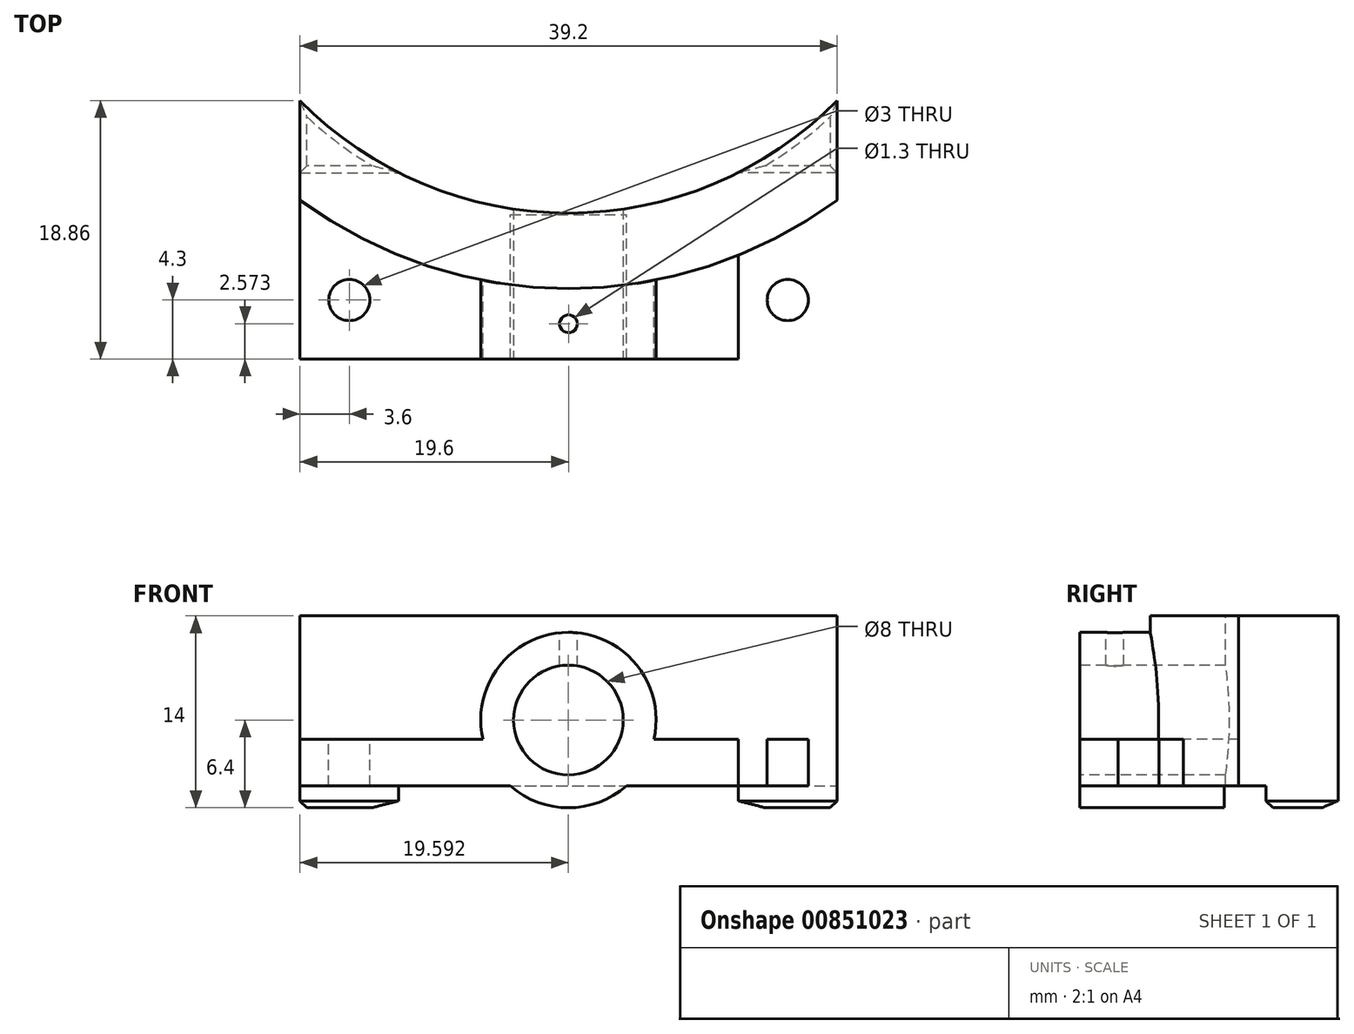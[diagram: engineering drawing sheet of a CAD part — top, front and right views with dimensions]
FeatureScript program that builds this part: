
annotation { "Feature Type Name" : "Feature", "Feature Type Description" : "" }
export const myFeature = defineFeature(function(context is Context, id is Id, definition is map)
    precondition{}
    {
        {
            var Q0;
            Q0=qCreatedBy(makeId("Top.planeOp"),FACE);
            var sketch = newSketch(context, id + "F0", { "sketchPlane" : qUnion([Q0])});
            skLineSegment(sketch, "E0", {"start": v(0, 0) * mm, "end": v(-16, 0) * mm, "construction": true});
            skCircle(sketch, "E1", {"center": v(-16, 0) * mm, "radius": 1.5 * mm});
            skLineSegment(sketch, "E2.bottom", {"start": v(-19.6, 9.3) * mm, "end": v(-12.4, 9.3) * mm});
            skLineSegment(sketch, "E2.top", {"start": v(-19.6, -9.3) * mm, "end": v(-12.4, -9.3) * mm});
            skLineSegment(sketch, "E2.left", {"start": v(-19.6, 9.3) * mm, "end": v(-19.6, -9.3) * mm});
            skLineSegment(sketch, "E2.right", {"start": v(-12.4, 9.3) * mm, "end": v(-12.4, -9.3) * mm});
            skLineSegment(sketch, "E3", {"start": v(0, 0) * mm, "end": v(0, 36.03) * mm, "construction": true});
            skCircle(sketch, "E4.MirrorC", {"center": v(16, 0) * mm, "radius": 1.5 * mm});
            skLineSegment(sketch, "E5.MirrorCS", {"start": v(19.6, 9.3) * mm, "end": v(19.6, -9.3) * mm});
            skLineSegment(sketch, "E6.MirrorCS", {"start": v(19.6, -9.3) * mm, "end": v(12.4, -9.3) * mm});
            skLineSegment(sketch, "E7.MirrorCS", {"start": v(19.6, 9.3) * mm, "end": v(12.4, 9.3) * mm});
            skLineSegment(sketch, "E8.MirrorCS", {"start": v(12.4, 9.3) * mm, "end": v(12.4, -9.3) * mm});
            skArc(sketch, "E9", {"start": v(0, 33.85) * mm, "mid": v(1.84, 32.82) * mm, "end": v(3.6, 31.66) * mm});
            skCircle(sketch, "E10", {"center": v(0, 33.85) * mm, "radius": 27.5 * mm});
            skLineSegment(sketch, "E11", {"start": v(-19.6, -4.3) * mm, "end": v(-12.4, -4.3) * mm});
            skLineSegment(sketch, "E12", {"start": v(-12.4, -4.3) * mm, "end": v(12.4, -4.3) * mm});
            skLineSegment(sketch, "E13", {"start": v(-19.6, 9.3) * mm, "end": v(-19.6, 14.56) * mm});
            skLineSegment(sketch, "E14", {"start": v(19.6, 9.3) * mm, "end": v(19.6, 14.56) * mm});
            skArc(sketch, "E15", {"start": v(-19.6, 7.3) * mm, "mid": v(0, 0.85) * mm, "end": v(19.6, 7.3) * mm});
            skLineSegment(sketch, "E16", {"start": v(12.4, -4.3) * mm, "end": v(19.6, -4.3) * mm});
            skSolve(sketch);
        }
        {
            var Q0;
            Q0=makeQuery(id+"F0.imprint","IMPRINT",FACE,{"disambiguationData":[TD([[makeQuery(id+"F0.imprint","IMPRINT",EDGE,{"derivedFrom":sQuery(id+"F0.wireOp",EDGE,"E1")}),-1.0]])]});
            var Q1;
            {var subQ1=sQuery(id+"F0.wireOp",EDGE,"E2.bottom");var subQ3=sQuery(id+"F0.wireOp",EDGE,"E15");var subQ4=makeQuery(id+"F0.imprint","INTERSECT",VERTEX,{"derivedFrom":[subQ1,subQ3]});Q1=makeQuery(id+"F0.imprint","IMPRINT",FACE,{"disambiguationData":[TD([[makeQuery(id+"F0.imprint","IMPRINT",EDGE,{"disambiguationData":[TD([[subQ4,-1.0]])],"derivedFrom":subQ3}),1.0]])]});}
            var Q2;
            {var subQ0=sQuery(id+"F0.wireOp",EDGE,"E13");var subQ3=sQuery(id+"F0.wireOp",EDGE,"E15");var subQ5=makeQuery(id+"F0.imprint","INTERSECT",VERTEX,{"derivedFrom":[subQ0,subQ3]});Q2=makeQuery(id+"F0.imprint","IMPRINT",FACE,{"disambiguationData":[TD([[makeQuery(id+"F0.imprint","IMPRINT",EDGE,{"disambiguationData":[TD([[subQ5,-1.0]])],"derivedFrom":subQ3}),-1.0]])]});}
            var Q3;
            {var subQ0=sQuery(id+"F0.wireOp",EDGE,"E12");Q3=makeQuery(id+"F0.imprint","IMPRINT",FACE,{"disambiguationData":[TD([[makeQuery(id+"F0.imprint","IMPRINT",EDGE,{"derivedFrom":subQ0}),1.0]])]});}
            var Q4;
            {var subQ1=sQuery(id+"F0.wireOp",EDGE,"E2.right");var subQ3=sQuery(id+"F0.wireOp",EDGE,"E15");var subQ4=makeQuery(id+"F0.imprint","INTERSECT",VERTEX,{"derivedFrom":[subQ1,subQ3]});Q4=makeQuery(id+"F0.imprint","IMPRINT",FACE,{"disambiguationData":[TD([[makeQuery(id+"F0.imprint","IMPRINT",EDGE,{"disambiguationData":[TD([[subQ4,-1.0]])],"derivedFrom":subQ3}),1.0]])]});}
            var Q5;
            {var subQ1=sQuery(id+"F0.wireOp",EDGE,"E7.MirrorCS");var subQ3=sQuery(id+"F0.wireOp",EDGE,"E15");var subQ4=makeQuery(id+"F0.imprint","INTERSECT",VERTEX,{"derivedFrom":[subQ1,subQ3]});Q5=makeQuery(id+"F0.imprint","IMPRINT",FACE,{"disambiguationData":[TD([[makeQuery(id+"F0.imprint","IMPRINT",EDGE,{"disambiguationData":[TD([[subQ4,1.0]])],"derivedFrom":subQ3}),1.0]])]});}
            var Q6;
            {var subQ0=sQuery(id+"F0.wireOp",EDGE,"E14");var subQ3=sQuery(id+"F0.wireOp",EDGE,"E15");var subQ5=makeQuery(id+"F0.imprint","INTERSECT",VERTEX,{"derivedFrom":[subQ0,subQ3]});Q6=makeQuery(id+"F0.imprint","IMPRINT",FACE,{"disambiguationData":[TD([[makeQuery(id+"F0.imprint","IMPRINT",EDGE,{"disambiguationData":[TD([[subQ5,1.0]])],"derivedFrom":subQ3}),-1.0]])]});}
            var Q7;
            Q7=makeQuery(id+"F0.imprint","IMPRINT",FACE,{"disambiguationData":[TD([[makeQuery(id+"F0.imprint","IMPRINT",EDGE,{"derivedFrom":sQuery(id+"F0.wireOp",EDGE,"E4.MirrorC")}),1.0]])]});
            extrude(context, id + "F1", {"entities" : qUnion([Q0, Q1, Q2, Q3, Q4, Q5, Q6, Q7]), "oppositeDirection" : true, "depth" : 3.4 * mm, "offsetDistance" : 25 * mm});
        }
        {
            var Q0;
            {var subQ0=sQuery(id+"F0.wireOp",EDGE,"E2.bottom");Q0=makeQuery(id+"F0.imprint","IMPRINT",FACE,{"disambiguationData":[TD([[makeQuery(id+"F0.imprint","IMPRINT",EDGE,{"derivedFrom":subQ0}),1.0]])]});}
            var Q1;
            {var subQ0=sQuery(id+"F0.wireOp",EDGE,"E7.MirrorCS");Q1=makeQuery(id+"F0.imprint","IMPRINT",FACE,{"disambiguationData":[TD([[makeQuery(id+"F0.imprint","IMPRINT",EDGE,{"derivedFrom":subQ0}),-1.0]])]});}
            extrude(context, id + "F2", {"entities" : qUnion([Q0, Q1]), "oppositeDirection" : true, "depth" : 5 * mm, "offsetDistance" : 25 * mm});
        }
        {
            var Q0;
            {var subQ0=sQuery(id+"F0.wireOp",EDGE,"E10");var subQ5=sQuery(id+"F0.wireOp",EDGE,"E13");var subQ6=makeQuery(id+"F0.imprint","INTERSECT",VERTEX,{"derivedFrom":[subQ0,subQ5]});Q0=makeQuery(id+"F0.imprint","IMPRINT",FACE,{"disambiguationData":[TD([[makeQuery(id+"F0.imprint","IMPRINT",EDGE,{"disambiguationData":[TD([[subQ6,1.0]])],"derivedFrom":subQ5}),-1.0]])]});}
            var Q1;
            {var subQ1=sQuery(id+"F0.wireOp",EDGE,"E2.bottom");var subQ3=sQuery(id+"F0.wireOp",EDGE,"E15");var subQ4=makeQuery(id+"F0.imprint","INTERSECT",VERTEX,{"derivedFrom":[subQ1,subQ3]});Q1=makeQuery(id+"F0.imprint","IMPRINT",FACE,{"disambiguationData":[TD([[makeQuery(id+"F0.imprint","IMPRINT",EDGE,{"disambiguationData":[TD([[subQ4,-1.0]])],"derivedFrom":subQ3}),1.0]])]});}
            var Q2;
            {var subQ1=sQuery(id+"F0.wireOp",EDGE,"E2.right");var subQ3=sQuery(id+"F0.wireOp",EDGE,"E15");var subQ4=makeQuery(id+"F0.imprint","INTERSECT",VERTEX,{"derivedFrom":[subQ1,subQ3]});Q2=makeQuery(id+"F0.imprint","IMPRINT",FACE,{"disambiguationData":[TD([[makeQuery(id+"F0.imprint","IMPRINT",EDGE,{"disambiguationData":[TD([[subQ4,-1.0]])],"derivedFrom":subQ3}),1.0]])]});}
            var Q3;
            {var subQ1=sQuery(id+"F0.wireOp",EDGE,"E7.MirrorCS");var subQ3=sQuery(id+"F0.wireOp",EDGE,"E15");var subQ4=makeQuery(id+"F0.imprint","INTERSECT",VERTEX,{"derivedFrom":[subQ1,subQ3]});Q3=makeQuery(id+"F0.imprint","IMPRINT",FACE,{"disambiguationData":[TD([[makeQuery(id+"F0.imprint","IMPRINT",EDGE,{"disambiguationData":[TD([[subQ4,1.0]])],"derivedFrom":subQ3}),1.0]])]});}
            var Q4;
            {var subQ0=sQuery(id+"F0.wireOp",EDGE,"E10");var subQ5=sQuery(id+"F0.wireOp",EDGE,"E14");var subQ6=makeQuery(id+"F0.imprint","INTERSECT",VERTEX,{"derivedFrom":[subQ0,subQ5]});Q4=makeQuery(id+"F0.imprint","IMPRINT",FACE,{"disambiguationData":[TD([[makeQuery(id+"F0.imprint","IMPRINT",EDGE,{"disambiguationData":[TD([[subQ6,1.0]])],"derivedFrom":subQ5}),1.0]])]});}
            extrude(context, id + "F3", {"entities" : qUnion([Q0, Q1, Q2, Q3, Q4]), "operationType" : NewBodyOperationType.ADD, "depth" : 9 * mm, "offsetDistance" : 25 * mm});
        }
        {
            var Q0;
            Q0=makeQuery(id+"F1.opExtrude","SWEPT_FACE",FACE,{"disambiguationData":[OSD([sQuery(id+"F0.wireOp",EDGE,"E11"),sQuery(id+"F0.wireOp",EDGE,"E12"),sQuery(id+"F0.wireOp",EDGE,"E16")])]});
            cPlane(context, id + "F4", {"entities" : qUnion([Q0]), "cplaneType" : CPlaneType.OFFSET, "offset" : 5.15 * mm, "oppositeDirection" : true, "width" : 150 * mm, "height" : 150 * mm});
        }
        {
            var Q0;
            Q0=qCreatedBy(id+"F4.planeOp",FACE);
            var sketch = newSketch(context, id + "F5", { "sketchPlane" : qUnion([Q0])});
            skLineSegment(sketch, "E17", {"start": v(0, 1.4) * mm, "end": v(0, 9.07) * mm, "construction": true});
            skCircle(sketch, "E18", {"center": v(0, 1.4) * mm, "radius": 4 * mm});
            skCircle(sketch, "E19", {"center": v(0, 1.4) * mm, "radius": 6.4 * mm});
            skSolve(sketch);
        }
        {
            var Q0;
            Q0=makeQuery(id+"F5.imprint","IMPRINT",FACE,{"disambiguationData":[TD([[makeQuery(id+"F5.imprint","IMPRINT",EDGE,{"derivedFrom":sQuery(id+"F5.wireOp",EDGE,"E18")}),1.0]])]});
            extrude(context, id + "F6", {"entities" : qUnion([Q0]), "operationType" : NewBodyOperationType.REMOVE, "endBound" : BoundingType.SYMMETRIC, "oppositeDirection" : true, "depth" : 25 * mm, "offsetDistance" : 25 * mm});
        }
        {
            var Q0;
            Q0=makeQuery(id+"F5.imprint","IMPRINT",FACE,{"disambiguationData":[TD([[makeQuery(id+"F5.imprint","IMPRINT",EDGE,{"derivedFrom":sQuery(id+"F5.wireOp",EDGE,"E18")}),-1.0]])]});
            extrude(context, id + "F7", {"entities" : qUnion([Q0]), "operationType" : NewBodyOperationType.ADD, "depth" : 5.15 * mm, "offsetDistance" : 25 * mm, "hasSecondDirection" : true, "secondDirectionOppositeDirection" : true, "secondDirectionDepth" : 5.4 * mm});
        }
        {
            var Q0;
            Q0=makeQuery(id+"F3.opExtrude","CAP_FACE",FACE,{"disambiguationData":[OSD([sQuery(id+"F0.wireOp",EDGE,"E2.left"),sQuery(id+"F0.wireOp",EDGE,"E5.MirrorCS"),sQuery(id+"F0.wireOp",EDGE,"E10"),sQuery(id+"F0.wireOp",EDGE,"E13"),sQuery(id+"F0.wireOp",EDGE,"E14"),sQuery(id+"F0.wireOp",EDGE,"E15")])],"isStart":false});
            var sketch = newSketch(context, id + "F8", { "sketchPlane" : qUnion([Q0])});
            skLineSegment(sketch, "E20", {"start": v(0, 6.35) * mm, "end": v(0, 0.85) * mm, "construction": true});
            skCircle(sketch, "E21", {"center": v(0, 3.6) * mm, "radius": 0.65 * mm});
            skLineSegment(sketch, "E22", {"start": v(0, 0.85) * mm, "end": v(0, -4.3) * mm, "construction": true});
            skCircle(sketch, "E23", {"center": v(0, -1.73) * mm, "radius": 0.65 * mm});
            skSolve(sketch);
        }
        {
            var Q0;
            Q0=makeQuery(id+"F8.imprint","IMPRINT",FACE,{"disambiguationData":[TD([[makeQuery(id+"F8.imprint","IMPRINT",EDGE,{"derivedFrom":sQuery(id+"F8.wireOp",EDGE,"E23")}),1.0]])]});
            extrude(context, id + "F9", {"entities" : qUnion([Q0]), "operationType" : NewBodyOperationType.REMOVE, "oppositeDirection" : true, "depth" : 5 * mm, "offsetDistance" : 25 * mm});
        }
        {
            var Q0;
            Q0=makeQuery(id+"F2.opExtrude","CAP_EDGE",EDGE,{"disambiguationData":[OSD([sQuery(id+"F0.wireOp",EDGE,"E14")])],"isStart":false});
            var Q1;
            Q1=makeQuery(id+"F2.opExtrude","CAP_EDGE",EDGE,{"disambiguationData":[OSD([sQuery(id+"F0.wireOp",EDGE,"E7.MirrorCS")])],"isStart":false});
            var Q2;
            {var subQ0=sQuery(id+"F0.wireOp",EDGE,"E10");Q2=makeQuery(id+"F2.opExtrude","CAP_EDGE",EDGE,{"disambiguationData":[OSD([subQ0]),TDD([makeQuery(id+"F0.imprint","IMPRINT",EDGE,{"disambiguationData":[TD([[makeQuery(id+"F0.imprint","INTERSECT",VERTEX,{"derivedFrom":[subQ0,sQuery(id+"F0.wireOp",EDGE,"E14")]}),1.0]])],"derivedFrom":subQ0})])],"isStart":false});}
            var Q3;
            {var subQ0=sQuery(id+"F0.wireOp",EDGE,"E10");Q3=makeQuery(id+"F2.opExtrude","CAP_EDGE",EDGE,{"disambiguationData":[OSD([subQ0]),TDD([makeQuery(id+"F0.imprint","IMPRINT",EDGE,{"disambiguationData":[TD([[makeQuery(id+"F0.imprint","INTERSECT",VERTEX,{"derivedFrom":[subQ0,sQuery(id+"F0.wireOp",EDGE,"E13")]}),-1.0]])],"derivedFrom":subQ0})])],"isStart":false});}
            var Q4;
            Q4=makeQuery(id+"F2.opExtrude","CAP_EDGE",EDGE,{"disambiguationData":[OSD([sQuery(id+"F0.wireOp",EDGE,"E2.bottom")])],"isStart":false});
            var Q5;
            Q5=makeQuery(id+"F2.opExtrude","CAP_EDGE",EDGE,{"disambiguationData":[OSD([sQuery(id+"F0.wireOp",EDGE,"E13")])],"isStart":false});
            chamfer(context, id + "F10", {"entities" : qUnion([Q0, Q1, Q2, Q3, Q4, Q5]), "width" : 0.5 * mm, "tangentPropagation" : true});
        }
    });
